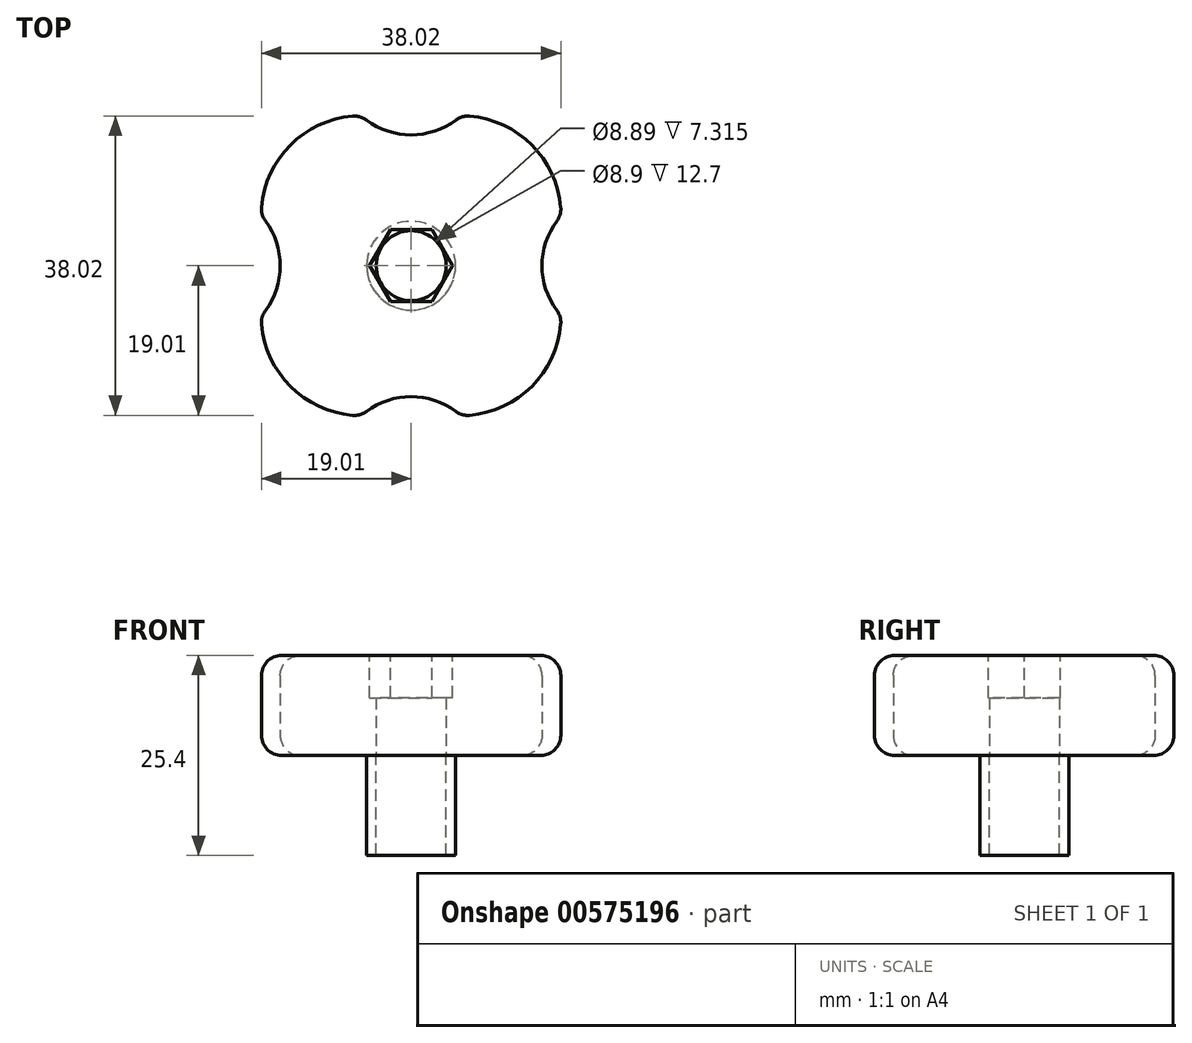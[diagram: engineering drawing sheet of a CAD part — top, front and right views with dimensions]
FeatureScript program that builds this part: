
annotation { "Feature Type Name" : "Feature", "Feature Type Description" : "" }
export const myFeature = defineFeature(function(context is Context, id is Id, definition is map)
    precondition{}
    {
        {
            var Q0;
            Q0=qCreatedBy(makeId("Top.planeOp"),FACE);
            var sketch = newSketch(context, id + "F0", { "sketchPlane" : qUnion([Q0])});
            skPoint(sketch, "E0.middle", {"position": v(0, 0) * mm});
            skPoint(sketch, "E1.visualSharp", {"position": v(-19.05, 19.05) * mm});
            skArc(sketch, "E1.filletArc", {"start": v(-6.35, 19.05) * mm, "mid": v(-15.33, 15.33) * mm, "end": v(-19.05, 6.35) * mm});
            skPoint(sketch, "E2.visualSharp", {"position": v(19.05, 19.05) * mm});
            skArc(sketch, "E2.filletArc", {"start": v(19.05, 6.35) * mm, "mid": v(15.33, 15.33) * mm, "end": v(6.35, 19.05) * mm});
            skPoint(sketch, "E3.visualSharp", {"position": v(19.05, -19.05) * mm});
            skArc(sketch, "E3.filletArc", {"start": v(6.35, -19.05) * mm, "mid": v(15.33, -15.33) * mm, "end": v(19.05, -6.35) * mm});
            skPoint(sketch, "E4.visualSharp", {"position": v(-19.05, -19.05) * mm});
            skArc(sketch, "E4.filletArc", {"start": v(-19.05, -6.35) * mm, "mid": v(-15.33, -15.33) * mm, "end": v(-6.35, -19.05) * mm});
            skArc(sketch, "E5", {"start": v(19.05, 6.35) * mm, "mid": v(16.62, 0) * mm, "end": v(19.05, -6.35) * mm});
            skArc(sketch, "E6", {"start": v(6.35, -19.05) * mm, "mid": v(0, -16.62) * mm, "end": v(-6.35, -19.05) * mm});
            skPoint(sketch, "E6.midSnap0", {"position": v(15.33, -15.33) * mm});
            skArc(sketch, "E7", {"start": v(-19.05, -6.35) * mm, "mid": v(-16.62, 0) * mm, "end": v(-19.05, 6.35) * mm});
            skArc(sketch, "E8", {"start": v(-6.35, 19.05) * mm, "mid": v(0, 16.62) * mm, "end": v(6.35, 19.05) * mm});
            skPoint(sketch, "E8.midSnap1", {"position": v(15.33, 15.33) * mm});
            skSolve(sketch);
        }
        {
            var Q0;
            Q0 = qSketchRegion(id + "F0", true);
            extrude(context, id + "F1", {"entities" : qUnion([Q0]), "depth" : 12.7 * mm, "offsetDistance" : 25.4 * mm});
        }
        {
            var Q0;
            Q0=makeQuery(id+"F1.opExtrude","CAP_FACE",FACE,{"disambiguationData":[OSD([sQuery(id+"F0.wireOp",EDGE,"E1.filletArc"),sQuery(id+"F0.wireOp",EDGE,"E2.filletArc"),sQuery(id+"F0.wireOp",EDGE,"E3.filletArc"),sQuery(id+"F0.wireOp",EDGE,"E4.filletArc"),sQuery(id+"F0.wireOp",EDGE,"E6"),sQuery(id+"F0.wireOp",EDGE,"E7"),sQuery(id+"F0.wireOp",EDGE,"E5"),sQuery(id+"F0.wireOp",EDGE,"E8")])],"isStart":false});
            var sketch = newSketch(context, id + "F2", { "sketchPlane" : qUnion([Q0])});
            skCircle(sketch, "E9.cCircle", {"center": v(0, 0) * mm, "radius": 4.57 * mm, "construction": true});
            skLineSegment(sketch, "E9.0", {"start": v(-2.64, 4.57) * mm, "end": v(2.64, 4.57) * mm});
            skLineSegment(sketch, "E9.1", {"start": v(2.64, 4.57) * mm, "end": v(5.28, 0) * mm});
            skLineSegment(sketch, "E9.2", {"start": v(5.28, 0) * mm, "end": v(2.64, -4.57) * mm});
            skLineSegment(sketch, "E9.3", {"start": v(2.64, -4.57) * mm, "end": v(-2.64, -4.57) * mm});
            skLineSegment(sketch, "E9.4", {"start": v(-2.64, -4.57) * mm, "end": v(-5.28, 0) * mm});
            skLineSegment(sketch, "E9.5", {"start": v(-5.28, 0) * mm, "end": v(-2.64, 4.57) * mm});
            skPoint(sketch, "E9.0.midPoint", {"position": v(0, 4.57) * mm});
            skSolve(sketch);
        }
        {
            var Q0;
            Q0 = qSketchRegion(id + "F2", true);
            extrude(context, id + "F3", {"entities" : qUnion([Q0]), "operationType" : NewBodyOperationType.REMOVE, "oppositeDirection" : true, "depth" : 5.38 * mm, "offsetDistance" : 25.4 * mm});
        }
        {
            var Q0;
            Q0=makeQuery(id+"F1.opExtrude","CAP_EDGE",EDGE,{"disambiguationData":[OSD([sQuery(id+"F0.wireOp",EDGE,"E8")])],"isStart":false});
            var Q1;
            Q1=makeQuery(id+"F1.opExtrude","CAP_EDGE",EDGE,{"disambiguationData":[OSD([sQuery(id+"F0.wireOp",EDGE,"E1.filletArc")])],"isStart":false});
            var Q2;
            Q2=makeQuery(id+"F1.opExtrude","CAP_EDGE",EDGE,{"disambiguationData":[OSD([sQuery(id+"F0.wireOp",EDGE,"E7")])],"isStart":false});
            var Q3;
            Q3=makeQuery(id+"F1.opExtrude","CAP_EDGE",EDGE,{"disambiguationData":[OSD([sQuery(id+"F0.wireOp",EDGE,"E4.filletArc")])],"isStart":false});
            var Q4;
            Q4=makeQuery(id+"F1.opExtrude","CAP_EDGE",EDGE,{"disambiguationData":[OSD([sQuery(id+"F0.wireOp",EDGE,"E6")])],"isStart":false});
            var Q5;
            Q5=makeQuery(id+"F1.opExtrude","CAP_EDGE",EDGE,{"disambiguationData":[OSD([sQuery(id+"F0.wireOp",EDGE,"E3.filletArc")])],"isStart":false});
            var Q6;
            Q6=makeQuery(id+"F1.opExtrude","CAP_EDGE",EDGE,{"disambiguationData":[OSD([sQuery(id+"F0.wireOp",EDGE,"E5")])],"isStart":false});
            var Q7;
            Q7=makeQuery(id+"F1.opExtrude","CAP_EDGE",EDGE,{"disambiguationData":[OSD([sQuery(id+"F0.wireOp",EDGE,"E2.filletArc")])],"isStart":false});
            var Q8;
            Q8=makeQuery(id+"F1.opExtrude","CAP_EDGE",EDGE,{"disambiguationData":[OSD([sQuery(id+"F0.wireOp",EDGE,"E3.filletArc")])],"isStart":true});
            var Q9;
            Q9=makeQuery(id+"F1.opExtrude","CAP_EDGE",EDGE,{"disambiguationData":[OSD([sQuery(id+"F0.wireOp",EDGE,"E6")])],"isStart":true});
            var Q10;
            Q10=makeQuery(id+"F1.opExtrude","CAP_EDGE",EDGE,{"disambiguationData":[OSD([sQuery(id+"F0.wireOp",EDGE,"E4.filletArc")])],"isStart":true});
            var Q11;
            Q11=makeQuery(id+"F1.opExtrude","CAP_EDGE",EDGE,{"disambiguationData":[OSD([sQuery(id+"F0.wireOp",EDGE,"E7")])],"isStart":true});
            var Q12;
            Q12=makeQuery(id+"F1.opExtrude","CAP_EDGE",EDGE,{"disambiguationData":[OSD([sQuery(id+"F0.wireOp",EDGE,"E1.filletArc")])],"isStart":true});
            var Q13;
            Q13=makeQuery(id+"F1.opExtrude","CAP_EDGE",EDGE,{"disambiguationData":[OSD([sQuery(id+"F0.wireOp",EDGE,"E8")])],"isStart":true});
            var Q14;
            Q14=makeQuery(id+"F1.opExtrude","CAP_EDGE",EDGE,{"disambiguationData":[OSD([sQuery(id+"F0.wireOp",EDGE,"E2.filletArc")])],"isStart":true});
            var Q15;
            Q15=makeQuery(id+"F1.opExtrude","CAP_EDGE",EDGE,{"disambiguationData":[OSD([sQuery(id+"F0.wireOp",EDGE,"E5")])],"isStart":true});
            var Q16;
            Q16=makeQuery(id+"F1.opExtrude","SWEPT_EDGE",EDGE,{"disambiguationData":[OSD([sQuery(id+"F0.wireOp",EDGE,"E2.filletArc"),sQuery(id+"F0.wireOp",EDGE,"E5"),sQuery(id+"F0.wireOp",EDGE,"E5")])]});
            var Q17;
            Q17=makeQuery(id+"F1.opExtrude","SWEPT_EDGE",EDGE,{"disambiguationData":[OSD([sQuery(id+"F0.wireOp",EDGE,"E3.filletArc"),sQuery(id+"F0.wireOp",EDGE,"E5"),sQuery(id+"F0.wireOp",EDGE,"E5")])]});
            var Q18;
            Q18=makeQuery(id+"F1.opExtrude","SWEPT_EDGE",EDGE,{"disambiguationData":[OSD([sQuery(id+"F0.wireOp",EDGE,"E1.filletArc"),sQuery(id+"F0.wireOp",EDGE,"E7")])]});
            var Q19;
            Q19=makeQuery(id+"F1.opExtrude","SWEPT_EDGE",EDGE,{"disambiguationData":[OSD([sQuery(id+"F0.wireOp",EDGE,"E3.filletArc"),sQuery(id+"F0.wireOp",EDGE,"E6")])]});
            var Q20;
            Q20=makeQuery(id+"F1.opExtrude","SWEPT_EDGE",EDGE,{"disambiguationData":[OSD([sQuery(id+"F0.wireOp",EDGE,"E4.filletArc"),sQuery(id+"F0.wireOp",EDGE,"E6")])]});
            var Q21;
            Q21=makeQuery(id+"F1.opExtrude","SWEPT_EDGE",EDGE,{"disambiguationData":[OSD([sQuery(id+"F0.wireOp",EDGE,"E2.filletArc"),sQuery(id+"F0.wireOp",EDGE,"E8")])]});
            fillet(context, id + "F4", {"entities" : qUnion([Q0, Q1, Q2, Q3, Q4, Q5, Q6, Q7, Q8, Q9, Q10, Q11, Q12, Q13, Q14, Q15, Q16, Q17, Q18, Q19, Q20, Q21]), "radius" : 2.54 * mm, "tangentPropagation" : true, "allowEdgeOverflow" : false});
        }
        {
            var Q0;
            Q0=makeQuery(id+"F1.opExtrude","SWEPT_EDGE",EDGE,{"disambiguationData":[OSD([sQuery(id+"F0.wireOp",EDGE,"E4.filletArc"),sQuery(id+"F0.wireOp",EDGE,"E7")])]});
            var Q1;
            Q1=makeQuery(id+"F1.opExtrude","SWEPT_EDGE",EDGE,{"disambiguationData":[OSD([sQuery(id+"F0.wireOp",EDGE,"E1.filletArc"),sQuery(id+"F0.wireOp",EDGE,"E8")])]});
            fillet(context, id + "F5", {"entities" : qUnion([Q0, Q1]), "radius" : 2.54 * mm, "tangentPropagation" : true, "allowEdgeOverflow" : false});
        }
        {
            var Q0;
            Q0=makeQuery(id+"F1.opExtrude","CAP_FACE",FACE,{"disambiguationData":[OSD([sQuery(id+"F0.wireOp",EDGE,"E1.filletArc"),sQuery(id+"F0.wireOp",EDGE,"E2.filletArc"),sQuery(id+"F0.wireOp",EDGE,"E3.filletArc"),sQuery(id+"F0.wireOp",EDGE,"E4.filletArc"),sQuery(id+"F0.wireOp",EDGE,"E6"),sQuery(id+"F0.wireOp",EDGE,"E7"),sQuery(id+"F0.wireOp",EDGE,"E5"),sQuery(id+"F0.wireOp",EDGE,"E8")])],"isStart":true});
            var sketch = newSketch(context, id + "F6", { "sketchPlane" : qUnion([Q0])});
            skCircle(sketch, "E10", {"center": v(0, 0) * mm, "radius": 4.45 * mm});
            skSolve(sketch);
        }
        {
            var Q0;
            Q0 = qSketchRegion(id + "F6", true);
            extrude(context, id + "F7", {"entities" : qUnion([Q0]), "operationType" : NewBodyOperationType.REMOVE, "oppositeDirection" : true, "depth" : 25.4 * mm, "offsetDistance" : 25.4 * mm});
        }
        {
            var Q0;
            Q0=makeQuery(id+"F1.opExtrude","CAP_FACE",FACE,{"disambiguationData":[OSD([sQuery(id+"F0.wireOp",EDGE,"E1.filletArc"),sQuery(id+"F0.wireOp",EDGE,"E2.filletArc"),sQuery(id+"F0.wireOp",EDGE,"E3.filletArc"),sQuery(id+"F0.wireOp",EDGE,"E4.filletArc"),sQuery(id+"F0.wireOp",EDGE,"E6"),sQuery(id+"F0.wireOp",EDGE,"E7"),sQuery(id+"F0.wireOp",EDGE,"E5"),sQuery(id+"F0.wireOp",EDGE,"E8")])],"isStart":true});
            var sketch = newSketch(context, id + "F8", { "sketchPlane" : qUnion([Q0])});
            skCircle(sketch, "E11", {"center": v(0, 0) * mm, "radius": 5.65 * mm});
            skSolve(sketch);
        }
        {
            var Q0;
            Q0 = qSketchRegion(id + "F8", true);
            extrude(context, id + "F9", {"entities" : qUnion([Q0]), "operationType" : NewBodyOperationType.ADD, "depth" : 12.7 * mm, "offsetDistance" : 25.4 * mm});
        }
        {
            var Q0;
            Q0=makeQuery(id+"F9.opExtrude","CAP_FACE",FACE,{"disambiguationData":[OSD([sQuery(id+"F8.wireOp",EDGE,"E11")])],"isStart":true});
            var sketch = newSketch(context, id + "F10", { "sketchPlane" : qUnion([Q0])});
            skCircle(sketch, "E12", {"center": v(0, 0) * mm, "radius": 4.45 * mm});
            skSolve(sketch);
        }
        {
            var Q0;
            Q0 = qSketchRegion(id + "F10", true);
            extrude(context, id + "F11", {"entities" : qUnion([Q0]), "operationType" : NewBodyOperationType.REMOVE, "oppositeDirection" : true, "depth" : 25.4 * mm, "offsetDistance" : 25.4 * mm});
        }
    });
